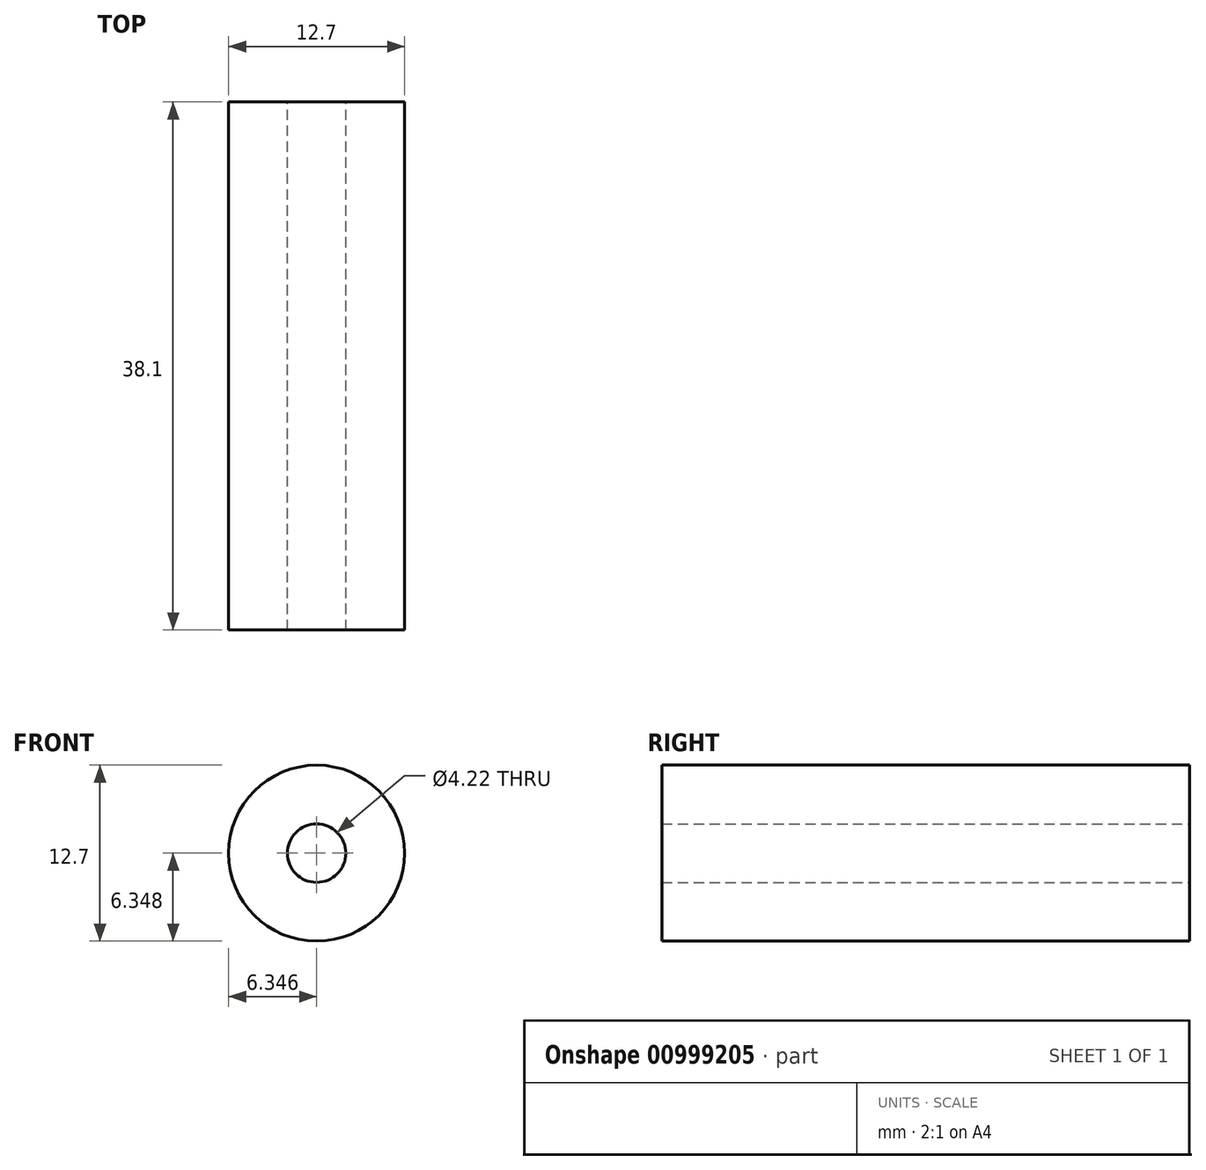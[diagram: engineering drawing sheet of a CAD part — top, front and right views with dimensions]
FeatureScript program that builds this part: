
annotation { "Feature Type Name" : "Feature", "Feature Type Description" : "" }
export const myFeature = defineFeature(function(context is Context, id is Id, definition is map)
    precondition{}
    {
        {
            var Q0;
            Q0=qCreatedBy(makeId("Front.planeOp"),FACE);
            var sketch = newSketch(context, id + "F0", { "sketchPlane" : qUnion([Q0])});
            skCircle(sketch, "E0", {"center": v(12.38, 66.88) * mm, "radius": 6.35 * mm});
            skCircle(sketch, "E1", {"center": v(12.38, 66.88) * mm, "radius": 2.1 * mm});
            skSolve(sketch);
        }
        {
            var Q0;
            Q0 = qSketchRegion(id + "F0", true);
            extrude(context, id + "F1", {"entities" : qUnion([Q0]), "depth" : 38.1 * mm, "offsetDistance" : 25.4 * mm});
        }
    });
